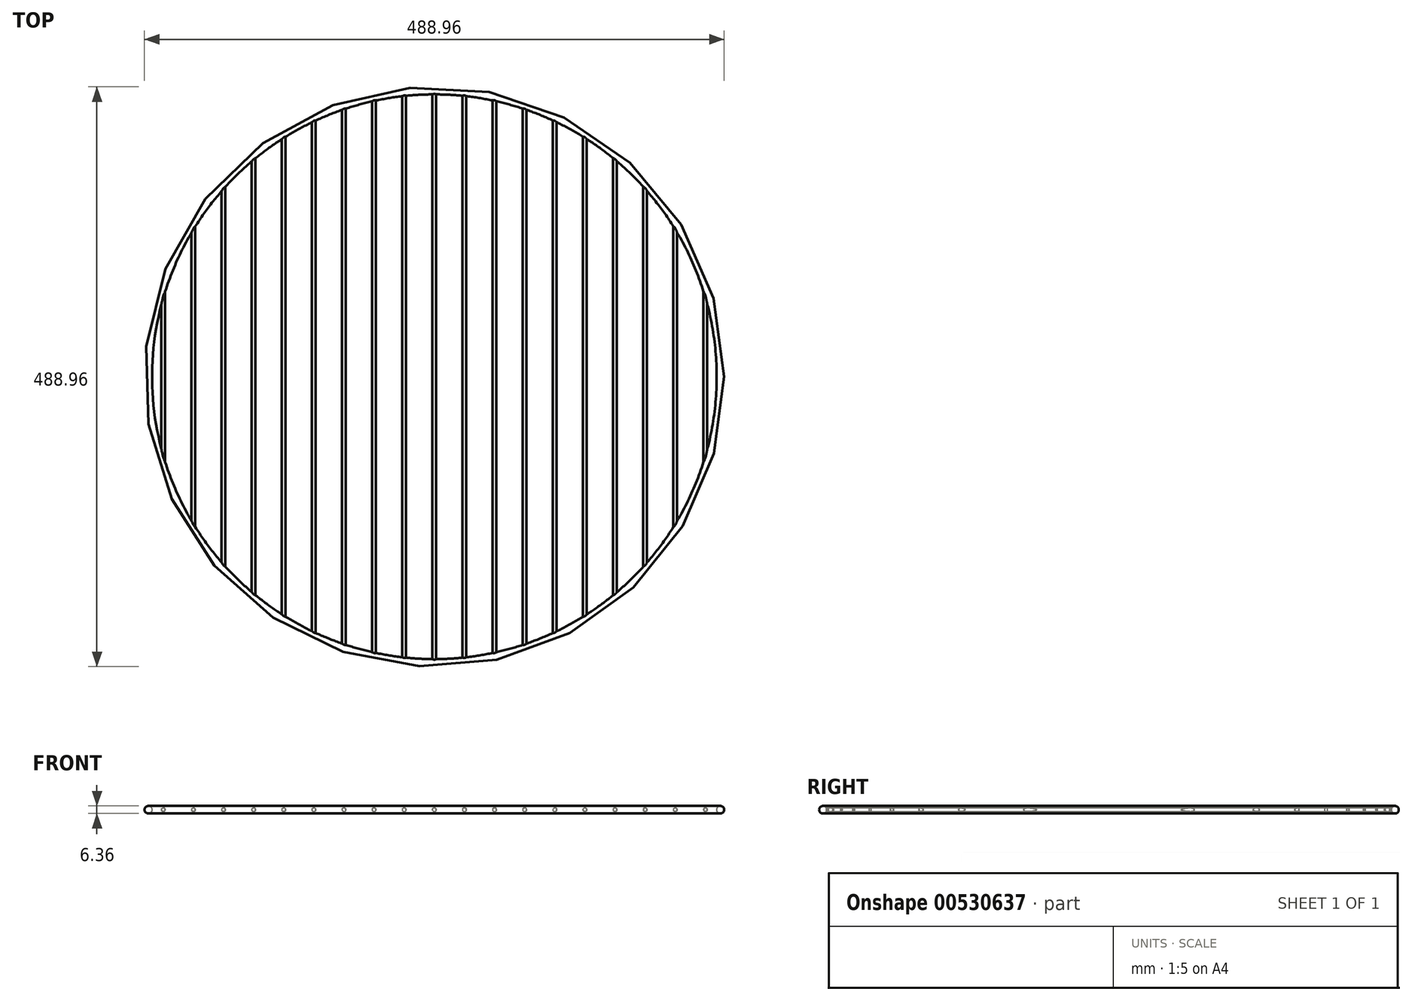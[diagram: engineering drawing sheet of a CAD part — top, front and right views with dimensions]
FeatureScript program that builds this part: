
annotation { "Feature Type Name" : "Feature", "Feature Type Description" : "" }
export const myFeature = defineFeature(function(context is Context, id is Id, definition is map)
    precondition{}
    {
        {
            var Q0;
            Q0=qCreatedBy(makeId("Front.planeOp"),FACE);
            var sketch = newSketch(context, id + "F0", { "sketchPlane" : qUnion([Q0])});
            skCircle(sketch, "E0", {"center": v(241.3, 0) * mm, "radius": 3.18 * mm});
            skLineSegment(sketch, "E1", {"start": v(0, 0) * mm, "end": v(0, 32.12) * mm, "construction": true});
            skSolve(sketch);
        }
        {
            var Q0;
            Q0=makeQuery(id+"F0.imprint","IMPRINT",FACE,{"disambiguationData":[TD([[makeQuery(id+"F0.imprint","IMPRINT",EDGE,{"derivedFrom":sQuery(id+"F0.wireOp",EDGE,"E0")}),1.0]])]});
            var Q1;
            Q1=sQuery(id+"F0.wireOp",EDGE,"E1");
            revolve(context, id + "F1", {"entities" : qUnion([Q0]), "axis" : qUnion([Q1]), "revolveType" : RevolveType.FULL});
        }
        {
            var Q0;
            Q0=qCreatedBy(makeId("Front.planeOp"),FACE);
            var sketch = newSketch(context, id + "F2", { "sketchPlane" : qUnion([Q0])});
            skCircle(sketch, "E2", {"center": v(0, 0) * mm, "radius": 1.59 * mm});
            skCircle(sketch, "E3.1.0.0", {"center": v(25.4, 0) * mm, "radius": 1.59 * mm});
            skCircle(sketch, "E3.2.0.0", {"center": v(50.8, 0) * mm, "radius": 1.59 * mm});
            skCircle(sketch, "E3.3.0.0", {"center": v(76.2, 0) * mm, "radius": 1.59 * mm});
            skCircle(sketch, "E3.4.0.0", {"center": v(101.6, 0) * mm, "radius": 1.59 * mm});
            skCircle(sketch, "E3.5.0.0", {"center": v(127, 0) * mm, "radius": 1.59 * mm});
            skCircle(sketch, "E3.6.0.0", {"center": v(152.4, 0) * mm, "radius": 1.59 * mm});
            skCircle(sketch, "E3.7.0.0", {"center": v(177.8, 0) * mm, "radius": 1.59 * mm});
            skCircle(sketch, "E3.8.0.0", {"center": v(203.2, 0) * mm, "radius": 1.59 * mm});
            skCircle(sketch, "E3.9.0.0", {"center": v(228.6, 0) * mm, "radius": 1.59 * mm});
            skLineSegment(sketch, "E3.direction1", {"start": v(0, 0) * mm, "end": v(25.4, 0) * mm, "construction": true});
            skCircle(sketch, "E4.1.0.0", {"center": v(-25.4, 0) * mm, "radius": 1.59 * mm});
            skCircle(sketch, "E4.2.0.0", {"center": v(-50.8, 0) * mm, "radius": 1.59 * mm});
            skCircle(sketch, "E4.3.0.0", {"center": v(-76.2, 0) * mm, "radius": 1.59 * mm});
            skCircle(sketch, "E4.4.0.0", {"center": v(-101.6, 0) * mm, "radius": 1.59 * mm});
            skCircle(sketch, "E4.5.0.0", {"center": v(-127, 0) * mm, "radius": 1.59 * mm});
            skCircle(sketch, "E4.6.0.0", {"center": v(-152.4, 0) * mm, "radius": 1.59 * mm});
            skCircle(sketch, "E4.7.0.0", {"center": v(-177.8, 0) * mm, "radius": 1.59 * mm});
            skCircle(sketch, "E4.8.0.0", {"center": v(-203.2, 0) * mm, "radius": 1.59 * mm});
            skCircle(sketch, "E4.9.0.0", {"center": v(-228.6, 0) * mm, "radius": 1.59 * mm});
            skLineSegment(sketch, "E4.direction1", {"start": v(0, 0) * mm, "end": v(-25.4, 0) * mm, "construction": true});
            skSolve(sketch);
        }
        {
            var Q0;
            Q0=qSketchRegion(id+"F2",true);
            extrude(context, id + "F3", {"entities" : qUnion([Q0]), "operationType" : NewBodyOperationType.ADD, "endBound" : BoundingType.UP_TO_NEXT, "depth" : 25.4 * mm, "hasSecondDirection" : true, "secondDirectionBound" : SecondDirectionBoundingType.UP_TO_NEXT, "secondDirectionOppositeDirection" : true, "secondDirectionDepth" : 25.4 * mm, "offsetDistance" : 25.4 * mm});
        }
    });
